# Revit family: Chair-Multi_Purpose-Allermuir-JoJo
name_source: partatom
category: Furniture
revit_build: Autodesk Revit Architecture 2012 (Build: 20110309_2315(x64)
units: mm (PartAtom-declared; Revit-internal decimal feet)

## types (3) — shared parameters
04 CSI = 12 51 00
2.5" Casters = No
95 CSI = 12510
Advanced Sync Tilt with Multi Position Back = No
Airflow Back Mesh = No
Assembly Code = E2020200
Back = Fabric - Allermuir - Upholstery - Lola - Smooth - Black
Base = Metal - Allermuir - Upholstery - Stainless - Brushed
Base or Frame = bright polished chrome, satin chrome or EPPC
Black Components = No
Black GRP Base = No
Black Gas Lift = No
Black Plastic Back Membrane = No
Color Availability = See price list for material options
Detachable writing table = No
Fabric Spec Sheets = http://www.allermuir.net
Height Adjustable Arms = No
Height Adjustable Arms with Multi funtction Pad = No
Lumbar Adjustment = No
Manufacturer = Allermuir
Manufacturer Fax = (419) 887 5805
Negative Seat Tilt = No
Overall Width = 18 115/128"
Plastic Arms in Black = NO
Plugin Data URL = http://products.ecoscorecard.com
Product Line = JoJo
Product Page URL = http://www.allermuir.com
Seat Depth Adjustment = No
Seat or Base = Fabric - Allermuir - Upholstery - Lola - Smooth - Black
Subcategory = Multi-Purpose
URL = http://www.allermuir.net
Upholstered Back = NO
Upholstered Seat = NO
ecoScorecard Product Page = http://products.ecoscorecard.com
ecoScorecard_data = http://thesenatorgroup.ecoscorecard.com

## per-type parameters (varying)
| type | A595 | A596 | A597 | Base Type | Description | Height Range | Overall Depth | Overall Height | Pedestal Base | Seat Height | Swaged Tubular Steel Legs | Weight |
| A595 | Yes | No | No |  | Centre pedestal high stool | 26.1"-30.9" | 16 115/128" | 35 51/128" | YES | 31" | NO | 31.9 lb |
| A596 | No | Yes | No | 4 Round steel tube frame | 4 leg high stool |  | 17 77/256" | 34 51/128" | NO | 30 1/2" | YES | 11.9 lb |
| A597 | No | No | Yes | 4 Round steel tube frame | Low stool |  | 16 115/128" | 22 205/256" |  | 19" | YES | 7.5 lb |

note: column(s) folded — value = type name in every type: Model

## geometry (parser evidence)
native form markers: Blend x6, Sweep x6
no freeform markers — native parametric forms only
